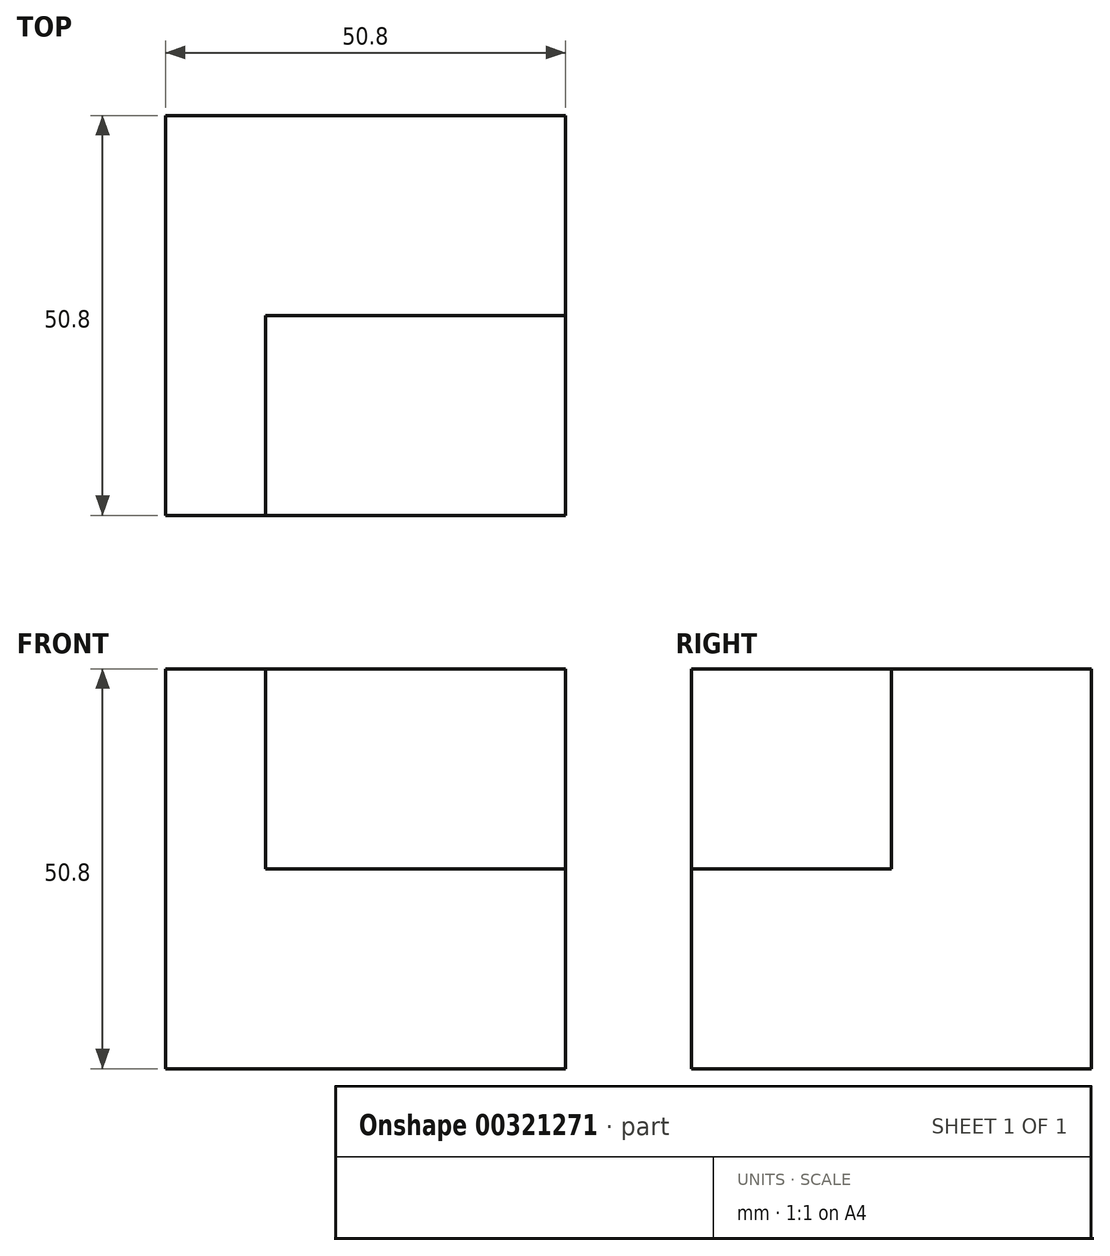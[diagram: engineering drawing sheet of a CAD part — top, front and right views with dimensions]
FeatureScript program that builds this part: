
annotation { "Feature Type Name" : "Feature", "Feature Type Description" : "" }
export const myFeature = defineFeature(function(context is Context, id is Id, definition is map)
    precondition{}
    {
        {
            var Q0;
            Q0=qCreatedBy(makeId("Right.planeOp"),FACE);
            var sketch = newSketch(context, id + "F0", { "sketchPlane" : qUnion([Q0])});
            skLineSegment(sketch, "E0", {"start": v(-16.3, -39.36) * mm, "end": v(34.5, -39.36) * mm});
            skLineSegment(sketch, "E1", {"start": v(-16.3, -39.36) * mm, "end": v(-16.3, 11.44) * mm});
            skLineSegment(sketch, "E2", {"start": v(-16.3, 11.44) * mm, "end": v(34.5, 11.44) * mm});
            skLineSegment(sketch, "E3", {"start": v(34.5, 11.44) * mm, "end": v(34.5, -39.36) * mm});
            skSolve(sketch);
        }
        {
            var Q0;
            Q0=makeQuery(id+"F0.imprint","IMPRINT",FACE,{"disambiguationData":[TD([[makeQuery(id+"F0.imprint","IMPRINT",EDGE,{"derivedFrom":sQuery(id+"F0.wireOp",EDGE,"E0")}),1.0]])]});
            extrude(context, id + "F1", {"entities" : qUnion([Q0]), "depth" : 50.8 * mm});
        }
        {
            var Q0;
            Q0=makeQuery(id+"F1.opExtrude","SWEPT_FACE",FACE,{"disambiguationData":[OSD([sQuery(id+"F0.wireOp",EDGE,"E1")])]});
            var sketch = newSketch(context, id + "F2", { "sketchPlane" : qUnion([Q0])});
            skLineSegment(sketch, "E4", {"start": v(12.7, 11.44) * mm, "end": v(12.7, -13.96) * mm});
            skLineSegment(sketch, "E5", {"start": v(12.7, -13.96) * mm, "end": v(50.8, -13.96) * mm});
            skLineSegment(sketch, "E6", {"start": v(50.8, -13.96) * mm, "end": v(50.8, 11.44) * mm});
            skLineSegment(sketch, "E7", {"start": v(50.8, 11.44) * mm, "end": v(12.7, 11.44) * mm});
            skSolve(sketch);
        }
        {
            var Q0;
            Q0=makeQuery(id+"F2.imprint","IMPRINT",FACE,{"disambiguationData":[TD([[makeQuery(id+"F2.imprint","IMPRINT",EDGE,{"derivedFrom":sQuery(id+"F2.wireOp",EDGE,"E4")}),1.0]])]});
            extrude(context, id + "F3", {"entities" : qUnion([Q0]), "operationType" : NewBodyOperationType.REMOVE, "oppositeDirection" : true, "depth" : 25.4 * mm});
        }
    });
